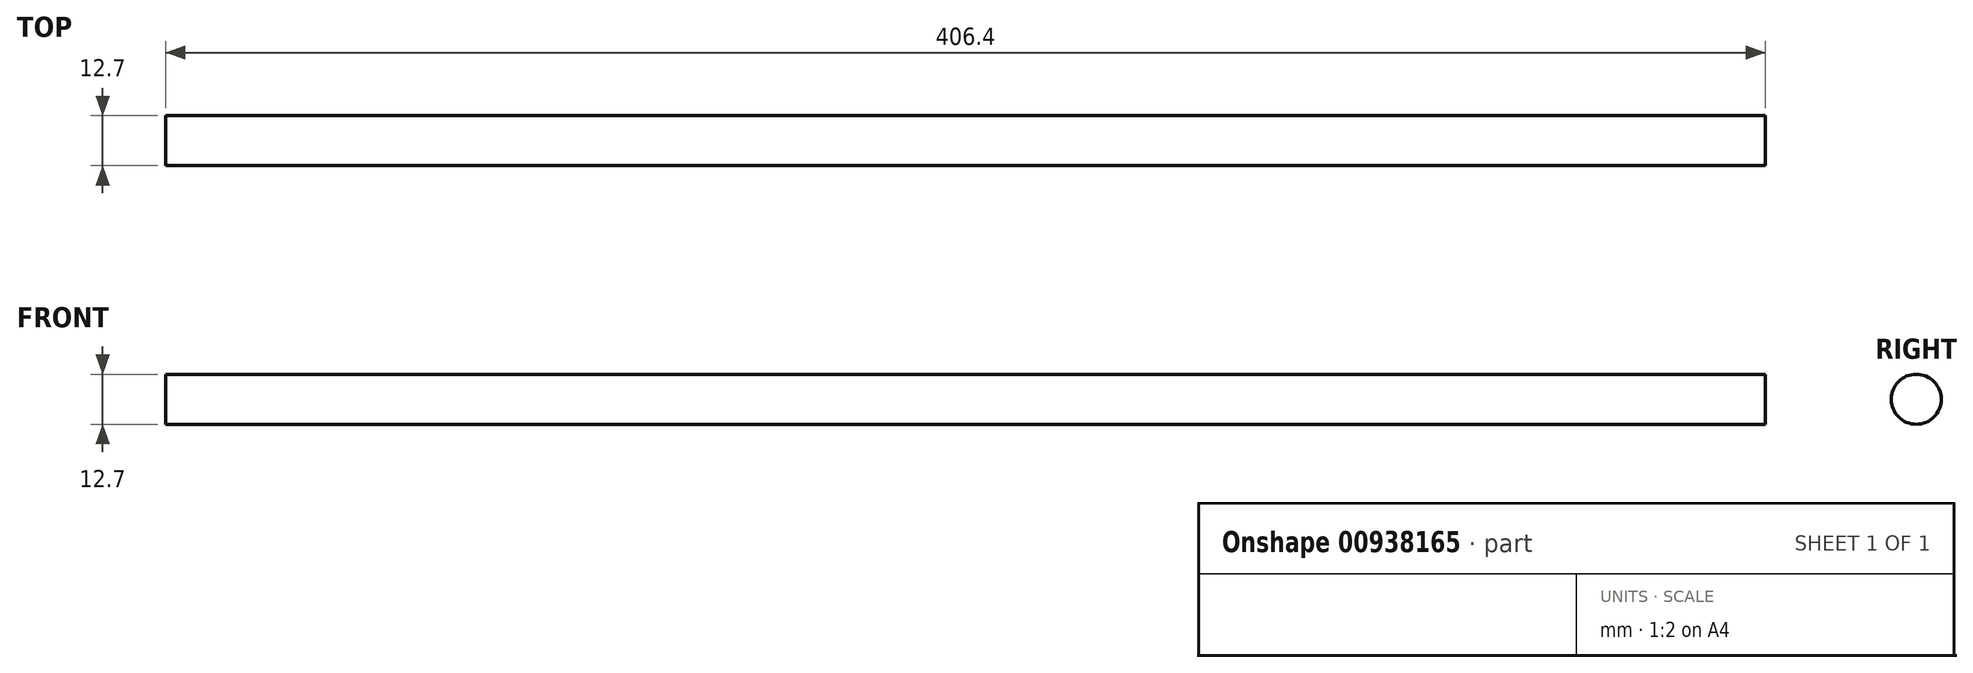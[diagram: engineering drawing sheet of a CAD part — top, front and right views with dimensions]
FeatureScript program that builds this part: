
annotation { "Feature Type Name" : "Feature", "Feature Type Description" : "" }
export const myFeature = defineFeature(function(context is Context, id is Id, definition is map)
    precondition{}
    {
        {
            var Q0;
            Q0=qCreatedBy(makeId("Right.planeOp"),FACE);
            var sketch = newSketch(context, id + "F0", { "sketchPlane" : qUnion([Q0])});
            skCircle(sketch, "E0", {"center": v(-51.86, 34.63) * mm, "radius": 6.35 * mm});
            skSolve(sketch);
        }
        {
            var Q0;
            Q0=makeQuery(id+"F0.imprint","IMPRINT",FACE,{"disambiguationData":[TD([[makeQuery(id+"F0.imprint","IMPRINT",EDGE,{"derivedFrom":sQuery(id+"F0.wireOp",EDGE,"E0")}),1.0]])]});
            extrude(context, id + "F1", {"entities" : qUnion([Q0]), "depth" : 406.4 * mm, "offsetDistance" : 25 * mm});
        }
    });
